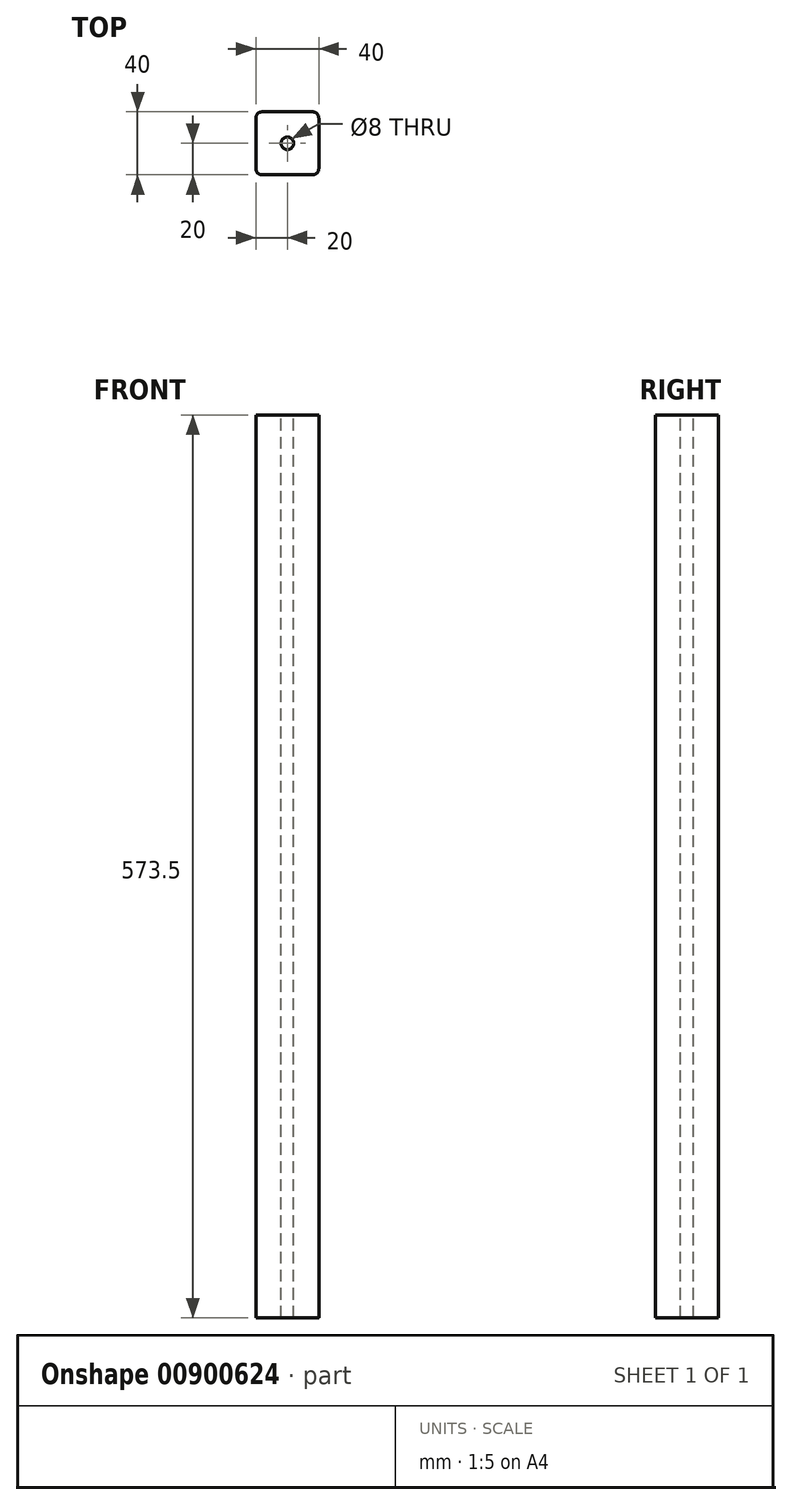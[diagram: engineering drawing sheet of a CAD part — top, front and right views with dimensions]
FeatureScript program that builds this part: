
annotation { "Feature Type Name" : "Feature", "Feature Type Description" : "" }
export const myFeature = defineFeature(function(context is Context, id is Id, definition is map)
    precondition{}
    {
        {
            var Q0;
            Q0=qCreatedBy(makeId("Top.planeOp"),FACE);
            var sketch = newSketch(context, id + "F0", { "sketchPlane" : qUnion([Q0])});
            skLineSegment(sketch, "E0.bottom", {"start": v(20, -20) * mm, "end": v(-20, -20) * mm});
            skLineSegment(sketch, "E0.top", {"start": v(20, 20) * mm, "end": v(-20, 20) * mm});
            skLineSegment(sketch, "E0.left", {"start": v(20, -20) * mm, "end": v(20, 20) * mm});
            skLineSegment(sketch, "E0.right", {"start": v(-20, -20) * mm, "end": v(-20, 20) * mm});
            skPoint(sketch, "E0.middle", {"position": v(0, 0) * mm});
            skSolve(sketch);
        }
        {
            var Q0;
            Q0=makeQuery(id+"F0.imprint","IMPRINT",FACE,{"disambiguationData":[TD([[makeQuery(id+"F0.imprint","IMPRINT",EDGE,{"derivedFrom":sQuery(id+"F0.wireOp",EDGE,"E0.bottom")}),-1.0]])]});
            extrude(context, id + "F1", {"entities" : qUnion([Q0]), "depth" : 573.5 * mm, "offsetDistance" : 25 * mm});
        }
        {
            var Q0;
            Q0=makeQuery(id+"F1.opExtrude","CAP_FACE",FACE,{"disambiguationData":[OSD([sQuery(id+"F0.wireOp",EDGE,"E0.bottom"),sQuery(id+"F0.wireOp",EDGE,"E0.top"),sQuery(id+"F0.wireOp",EDGE,"E0.left"),sQuery(id+"F0.wireOp",EDGE,"E0.right")])],"isStart":false});
            var sketch = newSketch(context, id + "F2", { "sketchPlane" : qUnion([Q0])});
            skPoint(sketch, "E1", {"position": v(0, 0) * mm});
            skSolve(sketch);
        }
        {
            var Q0;
            Q0=sQuery(id+"F2.wireOp",VERTEX,"E1");
            var Q1;
            Q1=makeQuery(id+"F1.opExtrude","SWEPT_BODY",BODY,{"disambiguationData":[OSD([sQuery(id+"F0.wireOp",EDGE,"E0.bottom"),sQuery(id+"F0.wireOp",EDGE,"E0.top"),sQuery(id+"F0.wireOp",EDGE,"E0.left"),sQuery(id+"F0.wireOp",EDGE,"E0.right")])]});
            hole(context, id + "F3", {"style" : HoleStyle.SIMPLE, "endStyle" : HoleEndStyle.THROUGH, "holeDiameter" : 8 * mm, "majorDiameter" : 5 * mm, "isTappedThrough" : true, "tappedDepth" : 12 * mm, "tapClearance" : 3, "locations" : qUnion([Q0]), "scope" : qUnion([Q1])});
        }
        {
            var Q0;
            Q0=makeQuery(id+"F1.opExtrude","SWEPT_EDGE",EDGE,{"disambiguationData":[OSD([sQuery(id+"F0.wireOp",EDGE,"E0.bottom"),sQuery(id+"F0.wireOp",EDGE,"E0.right")])]});
            var Q1;
            Q1=makeQuery(id+"F1.opExtrude","SWEPT_EDGE",EDGE,{"disambiguationData":[OSD([sQuery(id+"F0.wireOp",EDGE,"E0.bottom"),sQuery(id+"F0.wireOp",EDGE,"E0.left")])]});
            var Q2;
            Q2=makeQuery(id+"F1.opExtrude","SWEPT_EDGE",EDGE,{"disambiguationData":[OSD([sQuery(id+"F0.wireOp",EDGE,"E0.top"),sQuery(id+"F0.wireOp",EDGE,"E0.left")])]});
            var Q3;
            Q3=makeQuery(id+"F1.opExtrude","SWEPT_EDGE",EDGE,{"disambiguationData":[OSD([sQuery(id+"F0.wireOp",EDGE,"E0.top"),sQuery(id+"F0.wireOp",EDGE,"E0.right")])]});
            fillet(context, id + "F4", {"entities" : qUnion([Q0, Q1, Q2, Q3]), "radius" : 4 * mm, "tangentPropagation" : true, "allowEdgeOverflow" : false});
        }
    });
